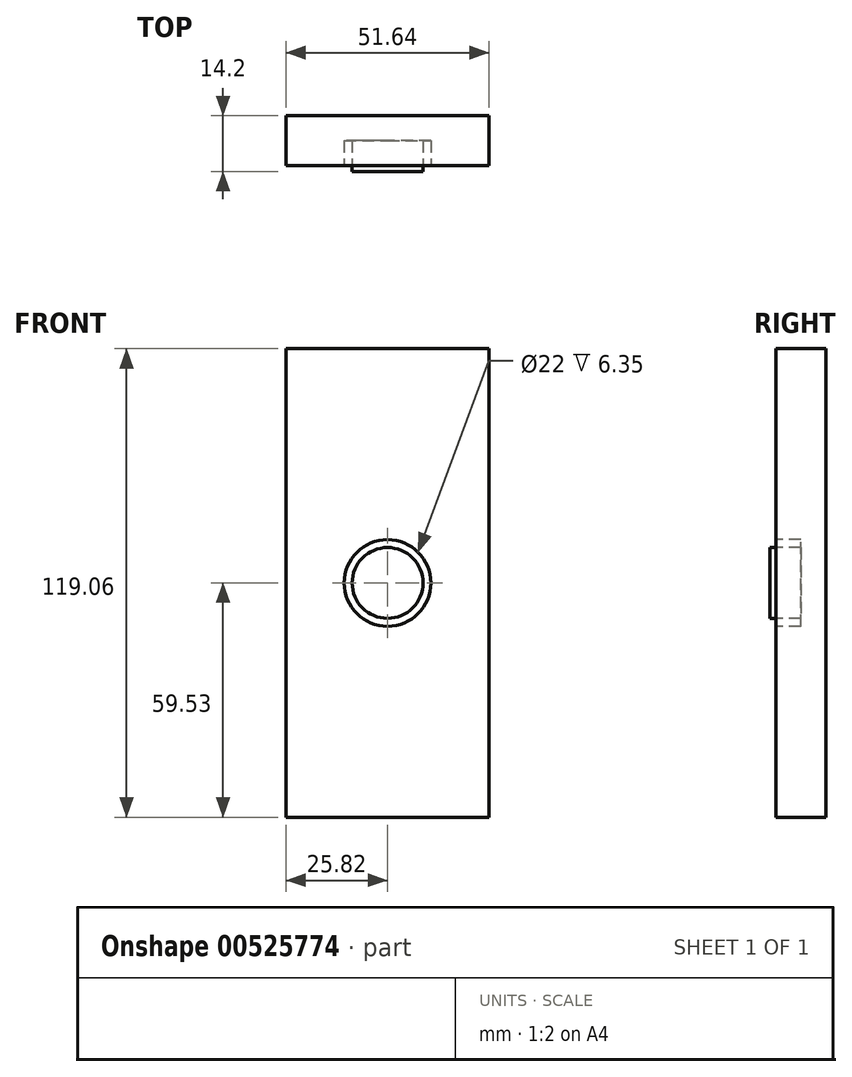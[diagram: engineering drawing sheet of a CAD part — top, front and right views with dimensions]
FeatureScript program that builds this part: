
annotation { "Feature Type Name" : "Feature", "Feature Type Description" : "" }
export const myFeature = defineFeature(function(context is Context, id is Id, definition is map)
    precondition{}
    {
        {
            var Q0;
            Q0=qCreatedBy(makeId("Front.planeOp"),FACE);
            var sketch = newSketch(context, id + "F0", { "sketchPlane" : qUnion([Q0])});
            skCircle(sketch, "E0", {"center": v(0, 0) * mm, "radius": 9 * mm});
            skSolve(sketch);
        }
        {
            var Q0;
            Q0=makeQuery(id+"F0.imprint","IMPRINT",FACE,{"disambiguationData":[TD([[makeQuery(id+"F0.imprint","IMPRINT",EDGE,{"derivedFrom":sQuery(id+"F0.wireOp",EDGE,"E0")}),1.0]])]});
            extrude(context, id + "F1", {"entities" : qUnion([Q0]), "oppositeDirection" : true, "depth" : 10 * mm, "offsetDistance" : 25.4 * mm, "hasSecondDirection" : true, "secondDirectionOppositeDirection" : false, "secondDirectionDepth" : 1.5 * mm});
        }
        {
            var Q0;
            Q0=qCreatedBy(makeId("Front.planeOp"),FACE);
            var sketch = newSketch(context, id + "F2", { "sketchPlane" : qUnion([Q0])});
            skCircle(sketch, "E1", {"center": v(0, 0) * mm, "radius": 11 * mm});
            skLineSegment(sketch, "E2.bottom", {"start": v(-25.82, 59.53) * mm, "end": v(25.82, 59.53) * mm});
            skLineSegment(sketch, "E2.top", {"start": v(-25.82, -59.53) * mm, "end": v(25.82, -59.53) * mm});
            skLineSegment(sketch, "E2.left", {"start": v(-25.82, 59.53) * mm, "end": v(-25.82, -59.53) * mm});
            skLineSegment(sketch, "E2.right", {"start": v(25.82, 59.53) * mm, "end": v(25.82, -59.53) * mm});
            skSolve(sketch);
        }
        {
            var Q0;
            Q0=makeQuery(id+"F2.imprint","IMPRINT",FACE,{"disambiguationData":[TD([[makeQuery(id+"F2.imprint","IMPRINT",EDGE,{"derivedFrom":sQuery(id+"F2.wireOp",EDGE,"E1")}),-1.0]])]});
            extrude(context, id + "F3", {"entities" : qUnion([Q0]), "oppositeDirection" : true, "depth" : 6.35 * mm, "offsetDistance" : 25.4 * mm});
        }
        {
            var Q0;
            Q0=makeQuery(id+"F3.opExtrude","CAP_FACE",FACE,{"disambiguationData":[OSD([sQuery(id+"F2.wireOp",EDGE,"E1"),sQuery(id+"F2.wireOp",EDGE,"E2.bottom"),sQuery(id+"F2.wireOp",EDGE,"E2.top"),sQuery(id+"F2.wireOp",EDGE,"E2.left"),sQuery(id+"F2.wireOp",EDGE,"E2.right")])],"isStart":false});
            var sketch = newSketch(context, id + "F4", { "sketchPlane" : qUnion([Q0])});
            skLineSegment(sketch, "E3.bottom", {"start": v(-25.82, 59.53) * mm, "end": v(25.82, 59.53) * mm});
            skLineSegment(sketch, "E3.top", {"start": v(-25.82, -59.53) * mm, "end": v(25.82, -59.53) * mm});
            skLineSegment(sketch, "E3.left", {"start": v(-25.82, 59.53) * mm, "end": v(-25.82, -59.53) * mm});
            skLineSegment(sketch, "E3.right", {"start": v(25.82, 59.53) * mm, "end": v(25.82, -59.53) * mm});
            skSolve(sketch);
        }
        {
            var Q0;
            Q0 = qSketchRegion(id + "F4", true);
            extrude(context, id + "F5", {"entities" : qUnion([Q0]), "operationType" : NewBodyOperationType.ADD, "depth" : 6.35 * mm, "offsetDistance" : 25.4 * mm});
        }
    });
